# Revit family: Plumbing-Urinals-Sloan-Valve-Weus-273630
name_source: partatom
category: Plumbing Fixtures
units: mm (PartAtom-declared; Revit-internal decimal feet)

## family parameters
Cut with Voids When Loaded = No
Host = Face
OmniClass Number = 23.45.05.21.11.21
OmniClass Title = Urinals
Part Type = Normal
Room Calculation Point = No
Round Connector Dimension = Use Diameter
Shared = No

## types (1)
- WEUS-1000.1301
    Apparent Load = 0 VA
    Assembly Code = D2010
    CWFU = 0
    Current = 0 A
    Default Elevation = 0 "
    Depth = 14.25 "
    Description = SU-1009 Urinal and ROYAL 186 ESS Flushometer.
    Edition number = 1
    Flush Rate = 0.125 GPF (0.5 LPF)
    Flushometer Code = 3452630
    Height = 25.5 "
    Keynote = 15410
    Manufacturer = Sloan Valve
    Model = WEUS-1000.1301
    Number of Poles = 3
    Operating Water Pressure = 15 – 80 PSI (103 – 552 kPa). Specific fixtures may require greater minimum flowing pressure - consult manufacturer requirements.
    Part Number = 10001301
    Power Factor = 0.8
    Product Material = Sloan Valve - Vitreous China - White
    Product data url = https://www.bimobject.com
    Sanitary Drain Connection Diameter = 2"
    URL = www.sloanvalve.com
    Urinal Code = 1101009
    Valve Pressure Drop = 0.00 psi
    Voltage = 24 V
    WFU = 0
    Water Inlet Connection Diameter = 1"
    Width = 17.25 "

## geometry (parser evidence)
native form markers: Sweep x6
no freeform markers — native parametric forms only
